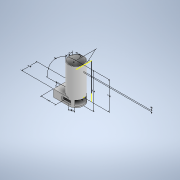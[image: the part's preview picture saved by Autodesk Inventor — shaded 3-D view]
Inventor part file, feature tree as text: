
AUTODESK INVENTOR PART (.ipt)
format: ipt  version: 2021 (Build 250183000, 183)  size: 408,064 bytes
history: native  units: in
note: dims shown in document units (in); Inventor stores cm internally (conversion verified against a paired STEP export)
features: other x15, sketch x13, extrude x9, plane x1
ambient origin geometry x8: Origin, YZ Plane, XZ Plane, XY Plane, X Axis, Y Axis, Z Axis, Center Point
bodies: Solid1 (feature_tree)
feature tree (38):
  other  "Annotations"
  sketch  "Sketch1"  dims[d0=2.7in d1=5.0in d2=0.0in]
  extrude  "BaseCup"  Depth=5.0in TaperAngle=0.0deg
  extrude  "Extrusion2"  Depth=5.3125in TaperAngle=0.0deg
  extrude  "Extrusion3"  Depth=1.3in TaperAngle=0.0deg
  plane  "Work Plane1"
  sketch  "Sketch5"  dims[d12=9.05in d13=0.0in d14=2.65in d15=0.0in]
  extrude  "Extrusion4"  Depth=2.25in
  extrude  "Extrusion5"  Depth=2.65in TaperAngle=0.0deg
  extrude  "Extrusion6"  Depth=1.0in
  extrude  "Extrusion7"  Depth=0.6in
  sketch  "Sketch12"  dims[d29=0.1in]
  sketch  "Sketch13"  dims[d30=0.2in]
  extrude  "Extrusion8"  Depth=1.0in
  extrude  "Extrusion9"  Depth=0.2in
  sketch  "Sketch2"  dims[d3=2.5in d4=5.3125in d5=0.0in]
  sketch  "Sketch3"  dims[d6=2.7in d7=1.3in d8=0.0in]
  sketch  "Sketch4"  dims[d10=0.95in d11=2.25in]
  sketch  "Sketch6"  dims[d17=3.9125in d18=0.0in d19=1.0in]
  sketch  "Sketch9"  dims[d20=1.5in d21=0.6in]
  sketch  "Sketch10"  dims[d22=3.4in d23=0.0in d26=1.0in]
  sketch  "Sketch11"  dims[d27=0.6in d28=0.2in]
  sketch  "Sketch14"  dims[d31=0.1in]
  sketch  "Sketch15"  dims[d32=0.6in d33=0.2in d34=0.1in d35=3.9in d36=0.0in d37=0.7in d38=0.9in d39=3.9in d40=0.0in d16=6.3in d24=0.306in d25=5.6588in d41=1.9381in d42=2.5in d43=5.0in d44=1.2in d45=0.2in d46=0.0in d47=0.3937in d48=2.7in d49=0.0in d50=0.3937in d51=2.65in d52=0.0014in d53=90.0deg d54=0.3129in d55=0.0404in d56=0.8775in d57=0.2102in d58=0.0in d59=0.0757in d60=0.3748in d61=1.35in d62=0.95in d9=1.3in]
  other  "Linear Dimension 1"
  other  "Linear Dimension 2"
  other  "Linear Dimension 3"
  other  "Diameter Dimension 1"
  other  "Linear Dimension 4"
  other  "Linear Dimension 5"
  other  "Linear Dimension 6"
  other  "Linear Dimension 7"
  other  "Linear Dimension 8"
  other  "Angular Dimension 1"
  other  "Linear Dimension 9"
  other  "Linear Dimension 10"
  other  "Radial Dimension 1"
  other  "Linear Dimension 11"
